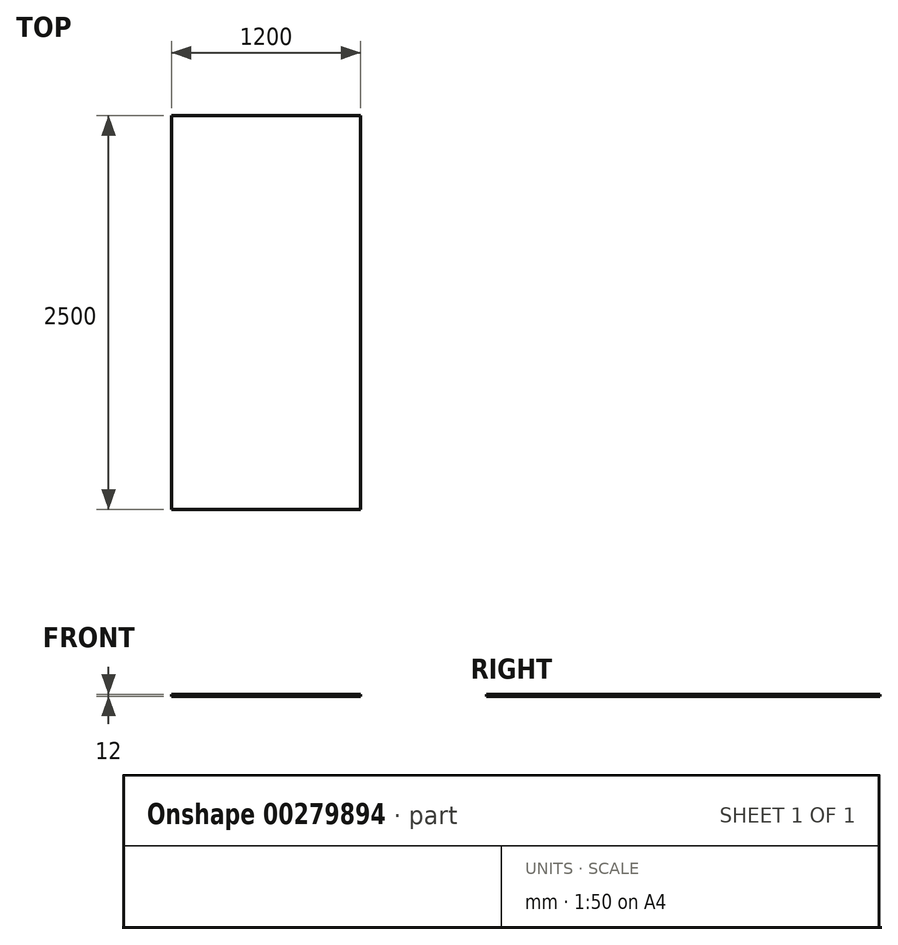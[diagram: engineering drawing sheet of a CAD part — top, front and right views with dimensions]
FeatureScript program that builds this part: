
annotation { "Feature Type Name" : "Feature", "Feature Type Description" : "" }
export const myFeature = defineFeature(function(context is Context, id is Id, definition is map)
    precondition{}
    {
        {
            var Q0;
            Q0=qCreatedBy(makeId("Top.planeOp"),FACE);
            var sketch = newSketch(context, id + "F0", { "sketchPlane" : qUnion([Q0])});
            skLineSegment(sketch, "E0.bottom", {"start": v(600, 1250) * mm, "end": v(-600, 1250) * mm});
            skLineSegment(sketch, "E0.top", {"start": v(600, -1250) * mm, "end": v(-600, -1250) * mm});
            skLineSegment(sketch, "E0.left", {"start": v(600, 1250) * mm, "end": v(600, -1250) * mm});
            skLineSegment(sketch, "E0.right", {"start": v(-600, 1250) * mm, "end": v(-600, -1250) * mm});
            skPoint(sketch, "E0.middle", {"position": v(0, 0) * mm});
            skSolve(sketch);
        }
        {
            var Q0;
            Q0=makeQuery(id+"F0.imprint","IMPRINT",FACE,{"disambiguationData":[TD([[makeQuery(id+"F0.imprint","IMPRINT",EDGE,{"derivedFrom":sQuery(id+"F0.wireOp",EDGE,"E0.bottom")}),1.0]])]});
            extrude(context, id + "F1", {"entities" : qUnion([Q0]), "depth" : 12 * mm});
        }
    });
